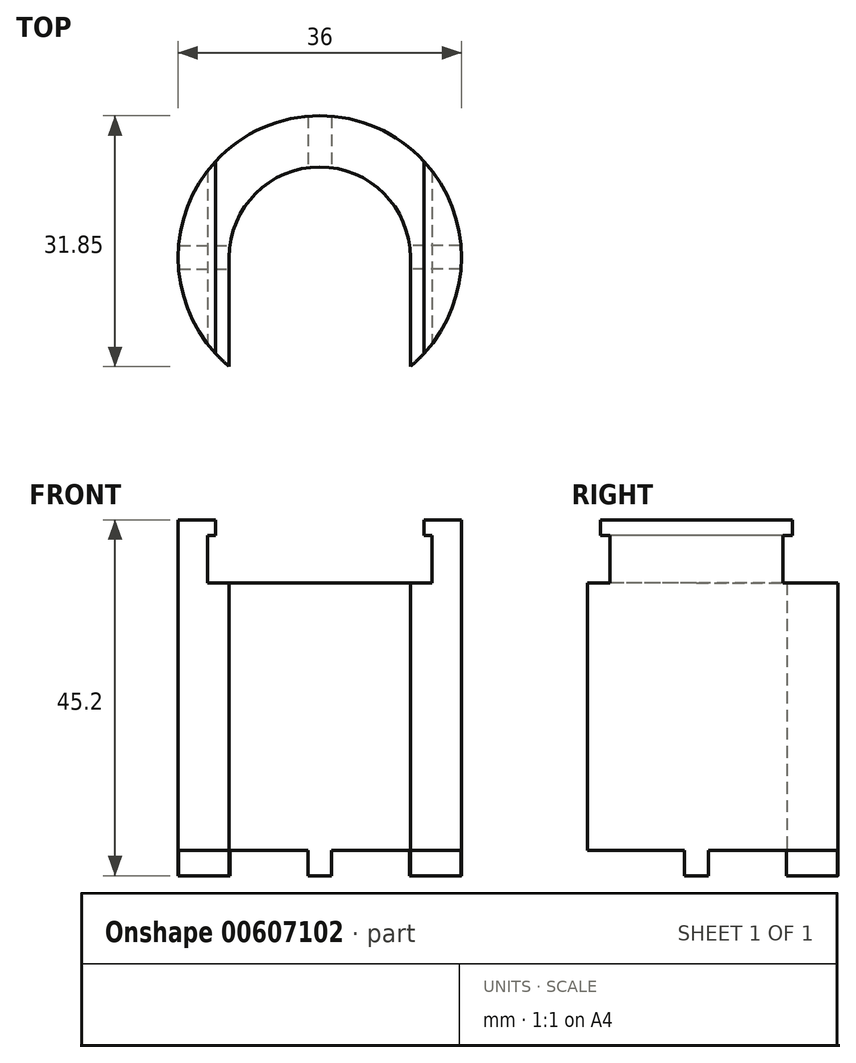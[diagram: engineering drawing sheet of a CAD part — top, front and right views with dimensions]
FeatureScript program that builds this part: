
annotation { "Feature Type Name" : "Feature", "Feature Type Description" : "" }
export const myFeature = defineFeature(function(context is Context, id is Id, definition is map)
    precondition{}
    {
        {
            var Q0;
            Q0=qCreatedBy(makeId("Top.planeOp"),FACE);
            var sketch = newSketch(context, id + "F0", { "sketchPlane" : qUnion([Q0])});
            skArc(sketch, "E0", {"start": v(11.5, -13.85) * mm, "mid": v(0, 18) * mm, "end": v(-11.5, -13.85) * mm});
            skArc(sketch, "E1", {"start": v(11.5, 0) * mm, "mid": v(0, 11.5) * mm, "end": v(-11.5, 0) * mm});
            skLineSegment(sketch, "E2", {"start": v(-11.5, 0) * mm, "end": v(-11.5, -13.85) * mm});
            skLineSegment(sketch, "E3", {"start": v(11.5, 0) * mm, "end": v(11.5, -13.85) * mm});
            skSolve(sketch);
        }
        {
            var Q0;
            Q0=qSketchRegion(id+"F0",true);
            extrude(context, id + "F1", {"entities" : qUnion([Q0]), "depth" : (25.5 + 19.7) * mm, "offsetDistance" : 25 * mm});
        }
        {
            var Q0;
            Q0=qCreatedBy(makeId("Front.planeOp"),FACE);
            var sketch = newSketch(context, id + "F2", { "sketchPlane" : qUnion([Q0])});
            skLineSegment(sketch, "E4.bottom", {"start": v(-14.25, 43.2) * mm, "end": v(14.25, 43.2) * mm});
            skLineSegment(sketch, "E4.top", {"start": v(-14.25, 37.2) * mm, "end": v(14.25, 37.2) * mm});
            skLineSegment(sketch, "E4.left", {"start": v(-14.25, 43.2) * mm, "end": v(-14.25, 37.2) * mm});
            skLineSegment(sketch, "E4.right", {"start": v(14.25, 43.2) * mm, "end": v(14.25, 37.2) * mm});
            skLineSegment(sketch, "E5", {"start": v(0, 0) * mm, "end": v(0, 37.1) * mm, "construction": true});
            skLineSegment(sketch, "E6", {"start": v(-13.25, 43.2) * mm, "end": v(-13.25, 45.2) * mm});
            skLineSegment(sketch, "E7", {"start": v(-13.25, 45.2) * mm, "end": v(13.25, 45.2) * mm});
            skLineSegment(sketch, "E8", {"start": v(13.25, 45.2) * mm, "end": v(13.25, 43.2) * mm});
            skSolve(sketch);
        }
        {
            var Q0;
            Q0=qSketchRegion(id+"F2",true);
            extrude(context, id + "F3", {"entities" : qUnion([Q0]), "operationType" : NewBodyOperationType.REMOVE, "endBound" : BoundingType.THROUGH_ALL, "oppositeDirection" : true, "depth" : 25 * mm, "offsetDistance" : 25 * mm});
        }
        {
            var Q0;
            Q0=qSketchRegion(id+"F2",true);
            extrude(context, id + "F4", {"entities" : qUnion([Q0]), "operationType" : NewBodyOperationType.REMOVE, "endBound" : BoundingType.THROUGH_ALL, "depth" : 25 * mm, "offsetDistance" : 25 * mm});
        }
        {
            var Q0;
            Q0=makeQuery(id+"F1.opExtrude","CAP_FACE",FACE,{"disambiguationData":[OSD([sQuery(id+"F0.wireOp",EDGE,"E0"),sQuery(id+"F0.wireOp",EDGE,"E1"),sQuery(id+"F0.wireOp",EDGE,"E2"),sQuery(id+"F0.wireOp",EDGE,"E3")])],"isStart":true});
            var sketch = newSketch(context, id + "F5", { "sketchPlane" : qUnion([Q0])});
            skLineSegment(sketch, "E9", {"start": v(-1.5, -17.94) * mm, "end": v(-1.5, -11.4) * mm});
            skArc(sketch, "E10.0", {"start": v(11.5, 0) * mm, "mid": v(0, -11.5) * mm, "end": v(-11.5, 0) * mm});
            skLineSegment(sketch, "E11", {"start": v(0, 0) * mm, "end": v(0, 9.82) * mm, "construction": true});
            skLineSegment(sketch, "E12.MirrorCS", {"start": v(1.5, -17.94) * mm, "end": v(1.5, -11.4) * mm});
            skArc(sketch, "E13.0", {"start": v(11.5, 13.85) * mm, "mid": v(0, -18) * mm, "end": v(-11.5, 13.85) * mm});
            skLineSegment(sketch, "E14", {"start": v(0, 0) * mm, "end": v(7.01, 0) * mm, "construction": true});
            skLineSegment(sketch, "E15", {"start": v(-17.94, 1.5) * mm, "end": v(-11.5, 1.5) * mm});
            skLineSegment(sketch, "E16.MirrorCS", {"start": v(-17.94, -1.5) * mm, "end": v(-11.4, -1.5) * mm});
            skLineSegment(sketch, "E17.0", {"start": v(-11.5, 0) * mm, "end": v(-11.5, 13.85) * mm});
            skLineSegment(sketch, "E17.1", {"start": v(11.5, 0) * mm, "end": v(11.5, 13.85) * mm});
            skPoint(sketch, "E18.orphan", {"position": v(-6.45, 1.5) * mm});
            skPoint(sketch, "E19.orphan", {"position": v(-6.45, -1.5) * mm});
            skPoint(sketch, "E20.orphan", {"position": v(-20.39, -1.5) * mm});
            skPoint(sketch, "E21.orphan", {"position": v(-20.39, 1.5) * mm});
            skPoint(sketch, "E22.orphan", {"position": v(-1.5, -8.05) * mm});
            skPoint(sketch, "E23.orphan", {"position": v(1.5, -8.05) * mm});
            skPoint(sketch, "E24.MirrorP", {"position": v(6.45, -1.5) * mm});
            skPoint(sketch, "E25.MirrorP", {"position": v(6.45, 1.5) * mm});
            skLineSegment(sketch, "E26.MirrorCS", {"start": v(17.94, -1.5) * mm, "end": v(11.4, -1.5) * mm});
            skPoint(sketch, "E27.MirrorP", {"position": v(20.39, -1.5) * mm});
            skLineSegment(sketch, "E28.MirrorCS", {"start": v(17.94, 1.5) * mm, "end": v(11.5, 1.5) * mm});
            skPoint(sketch, "E29.MirrorP", {"position": v(20.39, 1.5) * mm});
            skSolve(sketch);
        }
        {
            var Q0;
            {var subQ3=sQuery(id+"F5.wireOp",EDGE,"E15");Q0=makeQuery(id+"F5.imprint","IMPRINT",FACE,{"disambiguationData":[TD([[makeQuery(id+"F5.imprint","IMPRINT",EDGE,{"derivedFrom":subQ3}),1.0]])]});}
            var Q1;
            {var subQ0=sQuery(id+"F5.wireOp",EDGE,"E9");Q1=makeQuery(id+"F5.imprint","IMPRINT",FACE,{"disambiguationData":[TD([[makeQuery(id+"F5.imprint","IMPRINT",EDGE,{"derivedFrom":subQ0}),1.0]])]});}
            var Q2;
            {var subQ0=sQuery(id+"F5.wireOp",EDGE,"E12.MirrorCS");Q2=makeQuery(id+"F5.imprint","IMPRINT",FACE,{"disambiguationData":[TD([[makeQuery(id+"F5.imprint","IMPRINT",EDGE,{"derivedFrom":subQ0}),-1.0]])]});}
            var Q3;
            {var subQ3=sQuery(id+"F5.wireOp",EDGE,"E28.MirrorCS");Q3=makeQuery(id+"F5.imprint","IMPRINT",FACE,{"disambiguationData":[TD([[makeQuery(id+"F5.imprint","IMPRINT",EDGE,{"derivedFrom":subQ3}),-1.0]])]});}
            extrude(context, id + "F6", {"entities" : qUnion([Q0, Q1, Q2, Q3]), "operationType" : NewBodyOperationType.REMOVE, "oppositeDirection" : true, "depth" : 3.2 * mm, "offsetDistance" : 25 * mm});
        }
    });
